# Revit family: 0046372
name_source: partatom
category: Lighting Fixtures
revit_build: Autodesk Revit 2017 (Build: 20190507_1515(x64)
units: mm (PartAtom-declared; Revit-internal decimal feet)

## family parameters
Cut with Voids When Loaded = No
Host = Face
Light Source = Yes
OmniClass Number = 23.80.70.00
OmniClass Title = Lighting
Part Type = Normal
Room Calculation Point = No
Round Connector Dimension = Use Diameter
Shared = No

## types (4) — shared parameters
Apparent Load = 0 VA
Assembly Code = D5020200
AssetType = Fixed
ClassificationName = Uniclass2015
ClassificationValue = EF_70_80
Color Filter = 16777215
Default Elevation = 1219 mm
Dimming Lamp Color Temperature Shift = <None>
DocumentationLiterature = http://www.sylvania-lighting.com
ElectricShockClassification = Class I
Emit Shape Visible in Rendering = No
Emit from Circle Diameter = 610 mm
IfcExportAs = IfcLightFixtureType
IfcExportType = IfcLightFixtureType
ImpactProtectionIndex = IK08
IngressProtection = IP65
Keynote = 16500
LAM_D_SYL = 33 mm
LENGHT1_SYL = 686 mm  [stored 2.25066 ft]
LENGHT_-1_SYL = -686 mm  [stored -2.25066 ft]
Lamp = LED
LampColourRenderingIndex = 80
LampsType = LED
LuminousEfficacy = 136 lm/W
MID_W_DIST_SYL = 47 mm  [stored 0.154199 ft]
Manufacturer = Feilo Sylvania
ManufacturerName = Feilo Sylvania
Material_1_SYL = <By Category>
Material_2_SYL = <By Category>
Material_3_SYL = <By Category>
Material_4_SYL = <By Category>
NominalDepth = 67 mm
NominalHeight = 65 mm
NominalLength = 1403 mm  [stored 4.60302 ft]
Tilt Angle = -90.00°
Type Image = <None>
URL = http://www.sylvania-lighting.com
Voltage = 0 V
Weight = 11.16 kg
zero-valued in all types: Cost, PowerFactor

## per-type parameters (varying)
| type | Description | LampColourTemperature | LampNominalLuminous | Model | ModelNumber | ModelReference | Name | Photometric Web File | TypeName |
| 0046376 ST WTRPRF SLIM 1500 IP65 3800LM 865 | START Waterproof Slim is a LED integrated polycarbonate housing luminaire with easy to access electrical terminal through bayonet lock end caps and tool-free electrical connection due to push-in terminal. Flexible installation as mounting brackets can be positioned freely on the luminaire. 28W; 3800lm; High efficiency with 136lm/W and 100,000 hours lifespan L70B50. SDCM < 5; IP65; IK08; Class I; 1488mm x 70mm x 69mm. | 6500 K | 3800 lm | START Waterproof Slim 1500 IP65 3800lm 865 | 0046376 | START Waterproof Slim 1500 IP65 3800lm 865 | START Waterproof Slim 1500 IP65 3800lm 865 | 0046376.ies | START Waterproof Slim 1500 IP65 3800lm 865 |
| 0046372 ST WTRPRF SLIM 1500 IP65 7200LM 840 | START Waterproof Slim is a LED integrated polycarbonate housing luminaire with easy to access electrical terminal through bayonet lock end caps and tool-free electrical connection due to push-in terminal. Flexible installation as mounting brackets can be positioned freely on the luminaire. 53W; 7200lm; High efficiency with 136lm/W and 100,000 hours lifespan L70B50. SDCM < 5; IP65; IK08; Class I; 1488mm x 70mm x 69mm. | 4000 K | 7200 lm | START Waterproof Slim 1500 IP65 7200lm 840 | 0046372 | START Waterproof Slim 1500 IP65 7200lm 840 | START Waterproof Slim 1500 IP65 7200lm 840 | 0046372.ies | START Waterproof Slim 1500 IP65 7200lm 840 |
| 0046371 ST WTRPRF SLIM 1500 IP65 3800LM 840 | START Waterproof Slim is a LED integrated polycarbonate housing luminaire with easy to access electrical terminal through bayonet lock end caps and tool-free electrical connection due to push-in terminal. Flexible installation as mounting brackets can be positioned freely on the luminaire. 28W; 3800lm; High efficiency with 136lm/W and 100,000 hours lifespan L70B50. SDCM < 5; IP65; IK08; Class I; 1488mm x 70mm x 69mm. | 4000 K | 3800 lm | START Waterproof Slim 1500 IP65 3800lm 840 | 0046371 | START Waterproof Slim 1500 IP65 3800lm 840 | START Waterproof Slim 1500 IP65 3800lm 840 | 0046371.ies | START Waterproof Slim 1500 IP65 3800lm 840 |
| 0046377 ST WTRPRF SLIM 1500 IP65 7200LM 865 | START Waterproof Slim is a LED integrated polycarbonate housing luminaire with easy to access electrical terminal through bayonet lock end caps and tool-free electrical connection due to push-in terminal. Flexible installation as mounting brackets can be positioned freely on the luminaire. 53W; 7200lm; High efficiency with 136lm/W and 100,000 hours lifespan L70B50. SDCM < 5; IP65; IK08; Class I; 1488mm x 70mm x 69mm. | 6500 K | 7200 lm | START Waterproof Slim 1500 IP65 7200lm 865 | 0046377 | START Waterproof Slim 1500 IP65 7200lm 865 | START Waterproof Slim 1500 IP65 7200lm 865 | 0046377.ies | START Waterproof Slim 1500 IP65 7200lm 865 |

note: [stored X ft] marks values corroborated as IEEE doubles in the binary element streams (Revit-internal decimal feet)

## geometry (parser evidence)
native form markers: Sweep x3
no freeform markers — native parametric forms only
